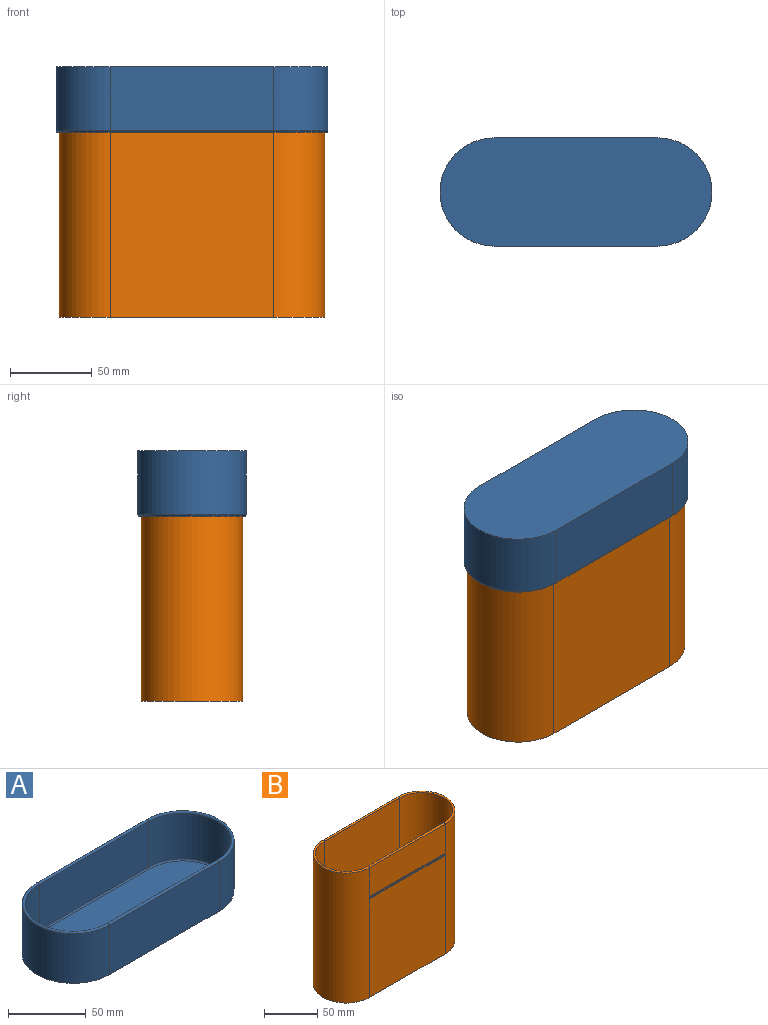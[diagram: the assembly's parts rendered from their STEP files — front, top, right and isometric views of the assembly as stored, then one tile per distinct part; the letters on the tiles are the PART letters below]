
ASSEMBLY  parts=2 mates=1
PART A: 18 faces, bbox 171.4x71.4x40 mm
  f0: plane 100x39mm, normal (0,1,0), area 3900mm2, adj f1,f3,f4,f15
  f1: cylinder r=33mm len=66mm, axis (0,0,-1), area 4043.2mm2, adj f0,f2,f4,f14
  f2: plane 100x39mm, normal (0,-1,0), area 3900mm2, adj f1,f3,f4,f16
  f3: cylinder r=33mm len=66mm, axis (0,0,-1), area 4043.2mm2, adj f0,f2,f4,f17
  f4: plane 166x66mm, normal (0,0,-1), area 10021.2mm2, adj f0,f1,f2,f3
  f5: plane 100x36mm, normal (0,-1,0), area 3600mm2, adj f6,f8,f11,f15
  f6: cylinder r=31mm len=62mm, axis (0,0,-1), area 3506mm2, adj f5,f7,f10,f14
  f7: plane 100x36mm, normal (0,1,0), area 3600mm2, adj f6,f8,f12,f16
  f8: cylinder r=31mm len=62mm, axis (0,0,-1), area 3506mm2, adj f5,f7,f13,f17
  f9: plane 160x60mm, normal (0,0,1), area 8827.4mm2, adj f10,f11,f12,f13
  f10: torus R=30mm, axis (0,0,1), area 151.2mm2, adj f6,f9,f11,f12
  f11: cylinder r=1mm len=100mm, axis (1,0,0), area 157.1mm2, adj f5,f9,f10,f13
  f12: cylinder r=1mm len=100mm, axis (-1,0,0), area 157.1mm2, adj f7,f9,f10,f13
  f13: torus R=30mm, axis (0,0,1), area 151.2mm2, adj f8,f9,f11,f12
  f14: torus R=32mm, axis (0,0,1), area 315.8mm2, adj f1,f6,f15,f16
  f15: cylinder r=1mm len=100mm, axis (1,0,0), area 314.2mm2, adj f0,f5,f14,f17
  f16: cylinder r=1mm len=100mm, axis (-1,0,0), area 314.2mm2, adj f2,f7,f14,f17
  f17: torus R=32mm, axis (0,0,1), area 315.8mm2, adj f3,f8,f15,f16
PART B: 20 faces, bbox 167.1x67.1x150 mm
  f0: plane 113x100mm, normal (0,-1,0), area 11300mm2, adj f1,f2,f4,f12
  f1: plane 162x62mm, normal (0,0,-1), area 9219.1mm2, adj f0,f2,f4,f5
  f2: cylinder r=31mm len=149mm, axis (0,0,1), area 14511mm2, adj f0,f1,f3,f5,f13,f19
  f3: plane 100x33.27mm, normal (0,-1,0), area 3326.8mm2, adj f2,f4,f15,f18
  f4: cylinder r=31mm len=149mm, axis (0,0,1), area 14511mm2, adj f0,f1,f3,f5,f11,f16
  f5: plane 149x100mm, normal (0,1,0), area 14900mm2, adj f1,f2,f4,f17
  f6: plane 158x58mm, normal (0,0,1), area 8442.1mm2, adj f7,f8,f9,f10
  f7: cylinder r=29mm len=147mm, axis (0,0,1), area 13392.6mm2, adj f6,f8,f10,f19
  f8: plane 147x100mm, normal (0,1,0), area 14700mm2, adj f6,f7,f9,f18
  f9: cylinder r=29mm len=147mm, axis (0,0,1), area 13392.6mm2, adj f6,f8,f10,f16
  f10: plane 147x100mm, normal (0,-1,0), area 14700mm2, adj f6,f7,f9,f17
  f11: plane 2.73x1mm, normal (1,0,0), area 1.5mm2, adj f4,f12,f14,f15
  f12: plane 100x1mm, normal (0,0,1), area 100mm2, adj f0,f11,f13,f14
  f13: plane 2.73x1mm, normal (-1,0,0), area 1.5mm2, adj f2,f12,f14,f15
  f14: plane 100x1mm, normal (0,-1,0), area 100mm2, adj f11,f12,f13,f15
  f15: cylinder r=2mm len=100mm, axis (-1,0,0), area 209.4mm2, adj f3,f11,f13,f14
  f16: torus R=30mm, axis (0,0,1), area 296.1mm2, adj f4,f9,f17,f18
  f17: cylinder r=1mm len=100mm, axis (-1,0,0), area 314.2mm2, adj f5,f10,f16,f19
  f18: cylinder r=1mm len=100mm, axis (1,0,0), area 314.2mm2, adj f3,f8,f16,f19
  f19: torus R=30mm, axis (0,0,1), area 296.1mm2, adj f2,f7,f17,f18
PLACE A rot(axis=(-1,0,0),180deg) t=(144.09,-86.31,-13.18)mm
PLACE B t=(144.09,-86.31,-16.18)mm
MATE slider B.f2 <-> A.f3  axis (0,0,1) through (194.09,-86.31,-16.18)mm
